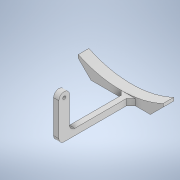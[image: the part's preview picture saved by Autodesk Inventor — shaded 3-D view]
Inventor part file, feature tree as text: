
AUTODESK INVENTOR PART (.ipt)
format: ipt  version: 2020 (Build 240168000, 168)  size: 326,656 bytes
history: native  units: mm
features: extrude x5, sketch x3, chamfer x2, fillet x2
ambient origin geometry x8: Origin, YZ Plane, XZ Plane, XY Plane, X Axis, Y Axis, Z Axis, Center Point
bodies: Solide1 (feature_tree)
feature tree (12):
  extrude  "Extrusion1"  Depth=15.0mm
  extrude  "Extrusion2"  Depth=80.0mm
  extrude  "Extrusion5"  Depth=10.0mm TaperAngle=0.0deg
  extrude  "Extrusion6"  Depth=5.0mm
  chamfer  "Chanfrein1"  Distance=80.0mm
  fillet  "Congé1"  Radius=6.0mm
  fillet  "Congé2"  Radius=67.9mm
  chamfer  "Chanfrein2"  Distance=4.6mm
  extrude  "Extrusion8"  Depth=6.0mm
  sketch  "Esquisse1"
  sketch  "Esquisse2"
  sketch  "Esquisse6"
